# Revit family: EZWSSM
name_source: partatom
category: Plumbing Fixtures
units: mm (PartAtom-declared; Revit-internal decimal feet)

## family parameters
Always vertical = Yes
Cut with Voids When Loaded = No
Part Type = Normal
Room Calculation Point = No
Round Connector Dimension = Use Diameter
Shared = No
Work Plane-Based = No

## types (1)
- EZWSSM
    Activation by = Electronic Bottle Filler Sensor
    Approx. Shipping Weight = 32 lbs
    Bubbler Style = No Bubbler
    Chilling Capacity = Non-refrigerated
    Dimensions (L x W x H) = 17 -15/16 inch x 8 -3/16 inch x 25-7/16 inch
    Finish = Stainless Steel
    Full Load Amps = 1
    Installation Location = Indoor
    Manufacturer = Elkay
    Model = EZWSSM
    Mounting Type = Wall Mount (On Wall)
    Number of Stations = 1
    Power = 115V/60Hz
    Rated Watts = 15
    Special Features = Antimicrobial, Green Ticker™, Hands Free, Laminar Flow, Real Drain
    Version = 1.0.0.0

## geometry (parser evidence)
native form markers: Sweep x9
no freeform markers — native parametric forms only
